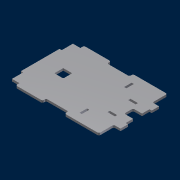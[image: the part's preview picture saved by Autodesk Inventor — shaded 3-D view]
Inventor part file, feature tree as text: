
AUTODESK INVENTOR PART (.ipt)
format: ipt  version: 2012 (Build 160160000, 160)  size: 187,904 bytes
history: native  units: mm
features: extrude x1, sketch x1
ambient origin geometry x8: Origin, YZ Plane, XZ Plane, XY Plane, X Axis, Y Axis, Z Axis, Center Point
feature tree (2):
  extrude  "Extrusion6"  Depth=10.0mm
  sketch  "Sketch1"  dims[d6=52.0mm d8=10.0mm d12=10.0mm d14=3.0mm d15=3.0mm d19=12.0mm d20=12.0mm d22=10.0mm d24=10.0mm d26=10.0mm d27=10.0mm d28=3.0mm d29=3.0mm d30=25.0mm d31=30.5mm d32=15.0mm d33=3.0mm d34=10.0mm d35=10.0mm d36=3.0mm d44=11.0mm d45=11.0mm d46=40.0mm d47=20.0mm d48=9.0mm d51=3.0mm d59=5.0mm d65=5.0mm d66=92.0mm d67=46.0mm d68=5.0mm d69=30.0mm d70=30.0mm d71=5.0mm d74=46.0mm d76=122.0mm d77=2.0mm d78=2.0mm d79=3.0mm d80=128.0mm d81=40.0mm d90=12.0mm d91=12.0mm d92=25.0mm d95=40.0mm d96=1.0mm d99=9.0mm d102=82.0mm d103=5.0mm d104=5.0mm d105=2.0mm d117=3.0mm d118=0.0mm]
